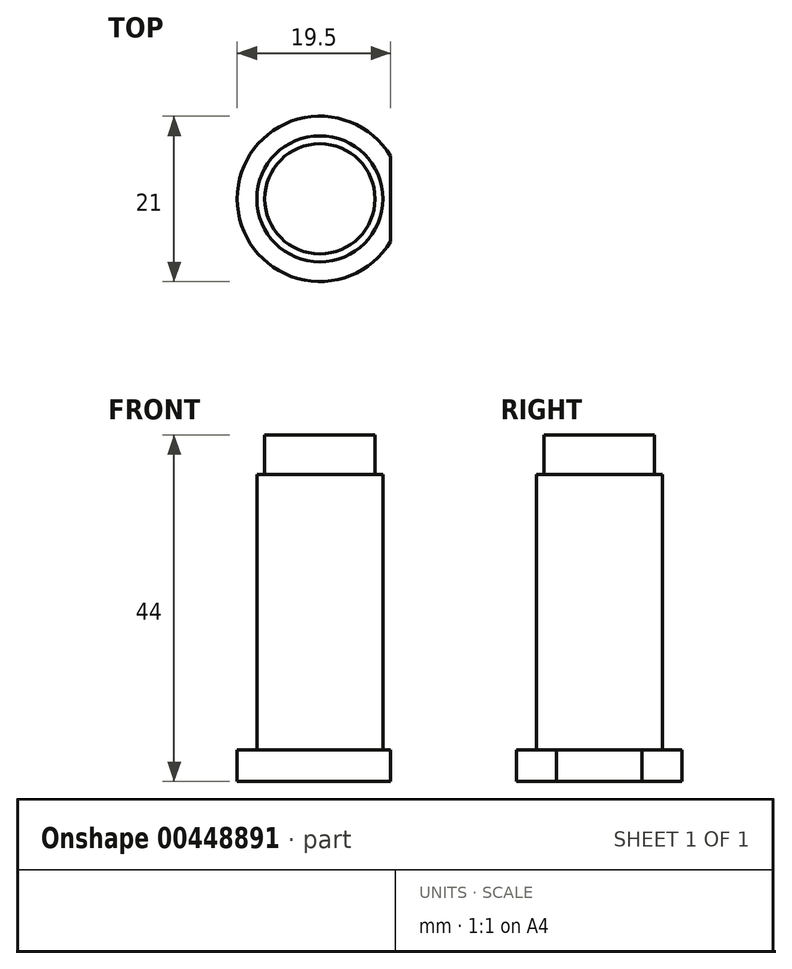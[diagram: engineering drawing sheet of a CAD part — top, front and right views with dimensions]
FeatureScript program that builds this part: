
annotation { "Feature Type Name" : "Feature", "Feature Type Description" : "" }
export const myFeature = defineFeature(function(context is Context, id is Id, definition is map)
    precondition{}
    {
        {
            var Q0;
            Q0=qCreatedBy(makeId("Top.planeOp"),FACE);
            var sketch = newSketch(context, id + "F0", { "sketchPlane" : qUnion([Q0])});
            skCircle(sketch, "E0", {"center": v(0, 0) * mm, "radius": 10.5 * mm});
            skSolve(sketch);
        }
        {
            var Q0;
            Q0=qSketchRegion(id+"F0",true);
            extrude(context, id + "F1", {"entities" : qUnion([Q0]), "depth" : 4 * mm});
        }
        {
            var Q0;
            Q0=qCreatedBy(makeId("Top.planeOp"),FACE);
            var sketch = newSketch(context, id + "F2", { "sketchPlane" : qUnion([Q0])});
            skCircle(sketch, "E1", {"center": v(0, 0) * mm, "radius": 8 * mm});
            skSolve(sketch);
        }
        {
            var Q0;
            Q0=qSketchRegion(id+"F2",true);
            extrude(context, id + "F3", {"entities" : qUnion([Q0]), "operationType" : NewBodyOperationType.ADD, "depth" : 39 * mm});
        }
        {
            var Q0;
            Q0=qCreatedBy(makeId("Right.planeOp"),FACE);
            var sketch = newSketch(context, id + "F4", { "sketchPlane" : qUnion([Q0])});
            skLineSegment(sketch, "E2", {"start": v(0, 44) * mm, "end": v(0, 39) * mm});
            skLineSegment(sketch, "E3", {"start": v(0, 39) * mm, "end": v(7, 39) * mm});
            skLineSegment(sketch, "E4", {"start": v(7, 39) * mm, "end": v(7, 44) * mm});
            skLineSegment(sketch, "E5", {"start": v(7, 44) * mm, "end": v(0, 44) * mm});
            skSolve(sketch);
        }
        {
            var Q0;
            Q0=makeQuery(id+"F4.imprint","IMPRINT",FACE,{"disambiguationData":[TD([[makeQuery(id+"F4.imprint","IMPRINT",EDGE,{"derivedFrom":sQuery(id+"F4.wireOp",EDGE,"E2")}),1.0]])]});
            var Q1;
            Q1=sQuery(id+"F4.wireOp",EDGE,"E2");
            revolve(context, id + "F5", {"operationType" : NewBodyOperationType.ADD, "entities" : qUnion([Q0]), "axis" : qUnion([Q1]), "revolveType" : RevolveType.FULL});
        }
        {
            var Q0;
            Q0=qCreatedBy(makeId("Top.planeOp"),FACE);
            var sketch = newSketch(context, id + "F6", { "sketchPlane" : qUnion([Q0])});
            skLineSegment(sketch, "E6.bottom", {"start": v(9, -10.52) * mm, "end": v(14.93, -10.52) * mm});
            skLineSegment(sketch, "E6.top", {"start": v(9, 10.61) * mm, "end": v(14.93, 10.61) * mm});
            skLineSegment(sketch, "E6.left", {"start": v(9, -10.52) * mm, "end": v(9, 10.61) * mm});
            skLineSegment(sketch, "E6.right", {"start": v(14.93, -10.52) * mm, "end": v(14.93, 10.61) * mm});
            skSolve(sketch);
        }
        {
            var Q0;
            Q0 = qSketchRegion(id + "F6", true);
            extrude(context, id + "F7", {"entities" : qUnion([Q0]), "operationType" : NewBodyOperationType.REMOVE, "depth" : 6 * mm});
        }
    });
